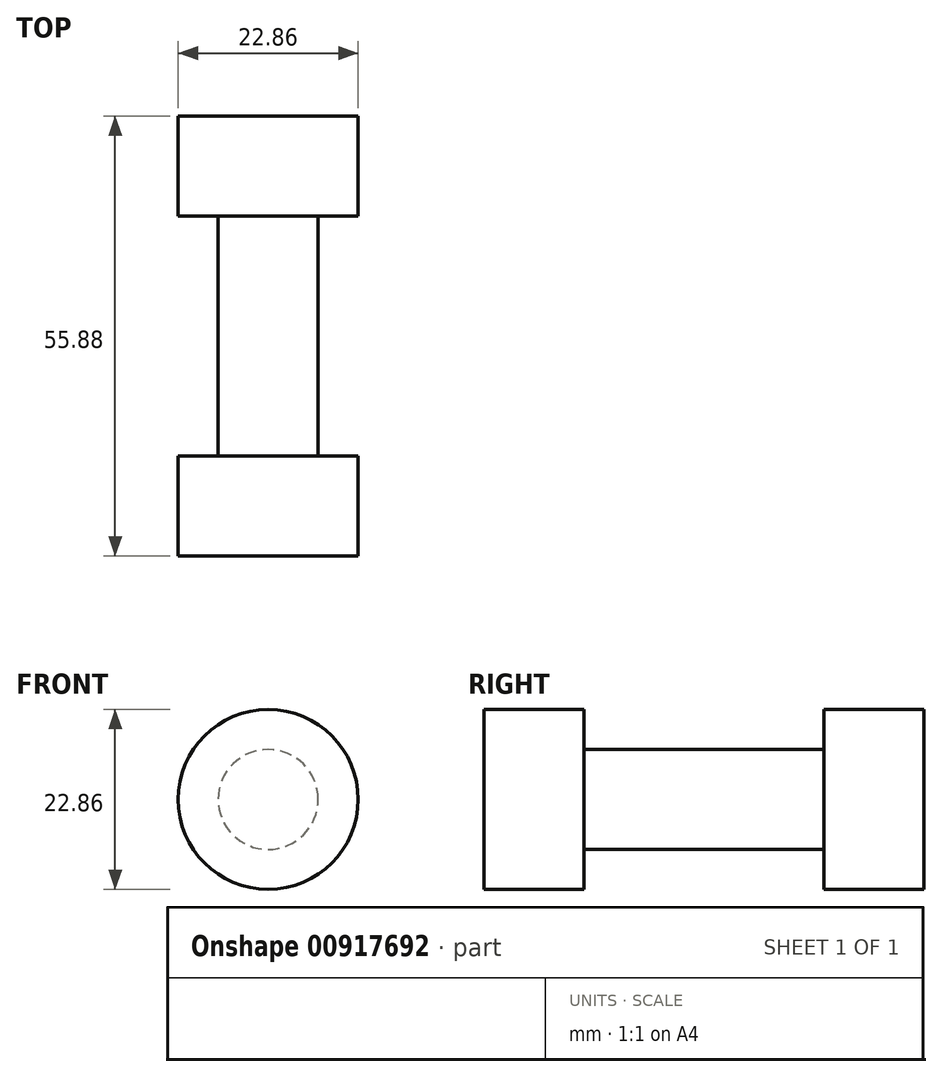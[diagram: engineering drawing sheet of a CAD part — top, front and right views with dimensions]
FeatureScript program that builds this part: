
annotation { "Feature Type Name" : "Feature", "Feature Type Description" : "" }
export const myFeature = defineFeature(function(context is Context, id is Id, definition is map)
    precondition{}
    {
        {
            var Q0;
            Q0=qCreatedBy(makeId("Front.planeOp"),FACE);
            var sketch = newSketch(context, id + "F0", { "sketchPlane" : qUnion([Q0])});
            skCircle(sketch, "E0", {"center": v(0, 0) * mm, "radius": 6.35 * mm});
            skSolve(sketch);
        }
        {
            var Q0;
            Q0=makeQuery(id+"F0.imprint","IMPRINT",FACE,{"disambiguationData":[TD([[makeQuery(id+"F0.imprint","IMPRINT",EDGE,{"derivedFrom":sQuery(id+"F0.wireOp",EDGE,"E0")}),1.0]])]});
            extrude(context, id + "F1", {"entities" : qUnion([Q0]), "depth" : 15.24 * mm, "offsetDistance" : 25.4 * mm});
        }
        {
            var Q0;
            Q0=makeQuery(id+"F1.opExtrude","CAP_FACE",FACE,{"disambiguationData":[OSD([sQuery(id+"F0.wireOp",EDGE,"E0")])],"isStart":false});
            var sketch = newSketch(context, id + "F2", { "sketchPlane" : qUnion([Q0])});
            skCircle(sketch, "E1", {"center": v(0, 0) * mm, "radius": 11.43 * mm});
            skSolve(sketch);
        }
        {
            var Q0;
            Q0=makeQuery(id+"F2.imprint","IMPRINT",FACE,{"disambiguationData":[TD([[makeQuery(id+"F2.imprint","IMPRINT",EDGE,{"derivedFrom":sQuery(id+"F2.wireOp",EDGE,"E1")}),1.0]])]});
            var Q1;
            Q1=makeQuery(id+"F2.imprint","IMPRINT",FACE,{"disambiguationData":[TD([[makeQuery(id+"F2.imprint","IMPRINT",EDGE,{"derivedFrom":makeQuery(id+"F1.opExtrude","CAP_EDGE",EDGE,{"disambiguationData":[OSD([sQuery(id+"F0.wireOp",EDGE,"E0")])],"isStart":false})}),1.0]])]});
            extrude(context, id + "F3", {"entities" : qUnion([Q0, Q1]), "operationType" : NewBodyOperationType.ADD, "depth" : 12.7 * mm, "offsetDistance" : 25.4 * mm});
        }
        {
            var Q0;
            Q0=makeQuery(id+"F1.opExtrude","SWEPT_BODY",BODY,{"disambiguationData":[OSD([sQuery(id+"F0.wireOp",EDGE,"E0")])]});
            var Q1;
            Q1=qCreatedBy(makeId("Front.planeOp"),FACE);
            mirror(context, id + "F4", {"operationType" : NewBodyOperationType.ADD, "entities" : qUnion([Q0]), "mirrorPlane" : qUnion([Q1])});
        }
    });
